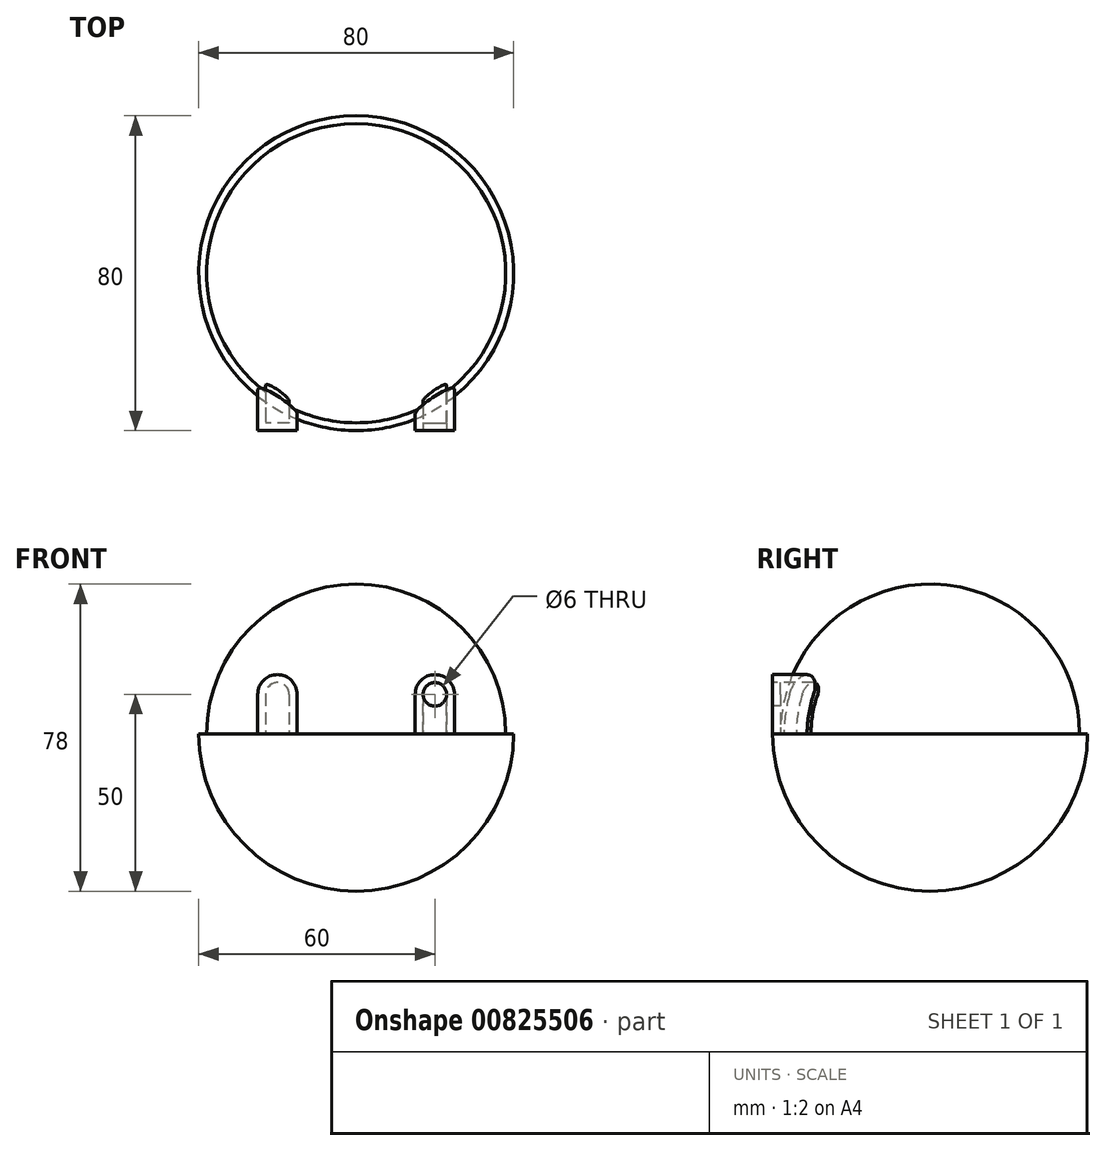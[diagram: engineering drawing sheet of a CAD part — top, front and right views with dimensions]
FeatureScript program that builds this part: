
annotation { "Feature Type Name" : "Feature", "Feature Type Description" : "" }
export const myFeature = defineFeature(function(context is Context, id is Id, definition is map)
    precondition{}
    {
        {
            var Q0;
            Q0=qCreatedBy(makeId("Top.planeOp"),FACE);
            var sketch = newSketch(context, id + "F0", { "sketchPlane" : qUnion([Q0])});
            skArc(sketch, "E0", {"start": v(0, -40) * mm, "mid": v(40, 0) * mm, "end": v(0, 40) * mm});
            skLineSegment(sketch, "E1", {"start": v(0, 40) * mm, "end": v(0, -40) * mm});
            skSolve(sketch);
        }
        {
            var Q0;
            Q0=makeQuery(id+"F0.imprint","IMPRINT",FACE,{"disambiguationData":[TD([[makeQuery(id+"F0.imprint","IMPRINT",EDGE,{"derivedFrom":sQuery(id+"F0.wireOp",EDGE,"E0")}),1.0]])]});
            var Q1;
            Q1=sQuery(id+"F0.wireOp",EDGE,"E1");
            revolve(context, id + "F1", {"surfaceOperationType" : NewSurfaceOperationType.NEW, "entities" : qUnion([Q0]), "axis" : qUnion([Q1]), "revolveType" : RevolveType.ONE_DIRECTION, "angle" : 180 * degree});
        }
        {
            var Q0;
            Q0=qCreatedBy(makeId("Front.planeOp"),FACE);
            cPlane(context, id + "F2", {"entities" : qUnion([Q0]), "cplaneType" : CPlaneType.OFFSET, "offset" : 40 * mm, "width" : 150 * mm, "height" : 150 * mm});
        }
        {
            var Q0;
            Q0=qCreatedBy(id+"F2.planeOp",FACE);
            var sketch = newSketch(context, id + "F3", { "sketchPlane" : qUnion([Q0])});
            skArc(sketch, "E2", {"start": v(25, 10) * mm, "mid": v(20, 15) * mm, "end": v(15, 10) * mm});
            skLineSegment(sketch, "E3", {"start": v(25, 10) * mm, "end": v(25, 0) * mm});
            skLineSegment(sketch, "E4", {"start": v(15, 10) * mm, "end": v(15, 0) * mm});
            skLineSegment(sketch, "E5", {"start": v(15, 0) * mm, "end": v(25, 0) * mm});
            skSolve(sketch);
        }
        {
            var Q0;
            Q0 = qSketchRegion(id + "F3", true);
            extrude(context, id + "F4", {"entities" : qUnion([Q0]), "operationType" : NewBodyOperationType.ADD, "oppositeDirection" : true, "depth" : 23.8 * mm, "offsetDistance" : 25 * mm});
        }
        {
            var Q0;
            Q0=makeQuery(id+"F1.opRevolve","SWEPT_BODY",BODY,{"disambiguationData":[OSD([sQuery(id+"F0.wireOp",EDGE,"E0"),sQuery(id+"F0.wireOp",EDGE,"E1")])]});
            var Q1;
            Q1=qCreatedBy(makeId("Right.planeOp"),FACE);
            mirror(context, id + "F5", {"operationType" : NewBodyOperationType.ADD, "entities" : qUnion([Q0]), "mirrorPlane" : qUnion([Q1])});
        }
        {
            var Q0;
            Q0=makeQuery(id+"F4.opExtrude","CAP_FACE",FACE,{"disambiguationData":[OSD([sQuery(id+"F3.wireOp",EDGE,"E2"),sQuery(id+"F3.wireOp",EDGE,"E3"),sQuery(id+"F3.wireOp",EDGE,"E4"),sQuery(id+"F3.wireOp",EDGE,"E5")])],"isStart":true});
            var sketch = newSketch(context, id + "F6", { "sketchPlane" : qUnion([Q0])});
            skCircle(sketch, "E6", {"center": v(20, 10) * mm, "radius": 3 * mm});
            skSolve(sketch);
        }
        {
            var Q0;
            {var subQ0=makeQuery(id+"F4.boolean.opBoolean","MERGE",FACE,{"derivedFrom":[makeQuery(id+"F1.opRevolve","CAP_FACE",FACE,{"disambiguationData":[OSD([sQuery(id+"F0.wireOp",EDGE,"E0"),sQuery(id+"F0.wireOp",EDGE,"E1")])],"isStart":true}),makeQuery(id+"F4.opExtrude","SWEPT_FACE",FACE,{"disambiguationData":[OSD([sQuery(id+"F3.wireOp",EDGE,"E5")])]})]});Q0=makeQuery(id+"F5.boolean.opBoolean","MERGE",FACE,{"derivedFrom":[subQ0,makeQuery(id+"F5.opPattern","COPY",FACE,{"derivedFrom":subQ0,"instanceName":"1"})]});}
            shell(context, id + "F7", {"entities" : qUnion([Q0]), "thickness" : 2 * mm});
        }
        {
            var Q0;
            Q0 = qSketchRegion(id + "F6", true);
            extrude(context, id + "F8", {"entities" : qUnion([Q0]), "operationType" : NewBodyOperationType.REMOVE, "oppositeDirection" : true, "depth" : 24 * mm, "offsetDistance" : 25 * mm});
        }
    });
